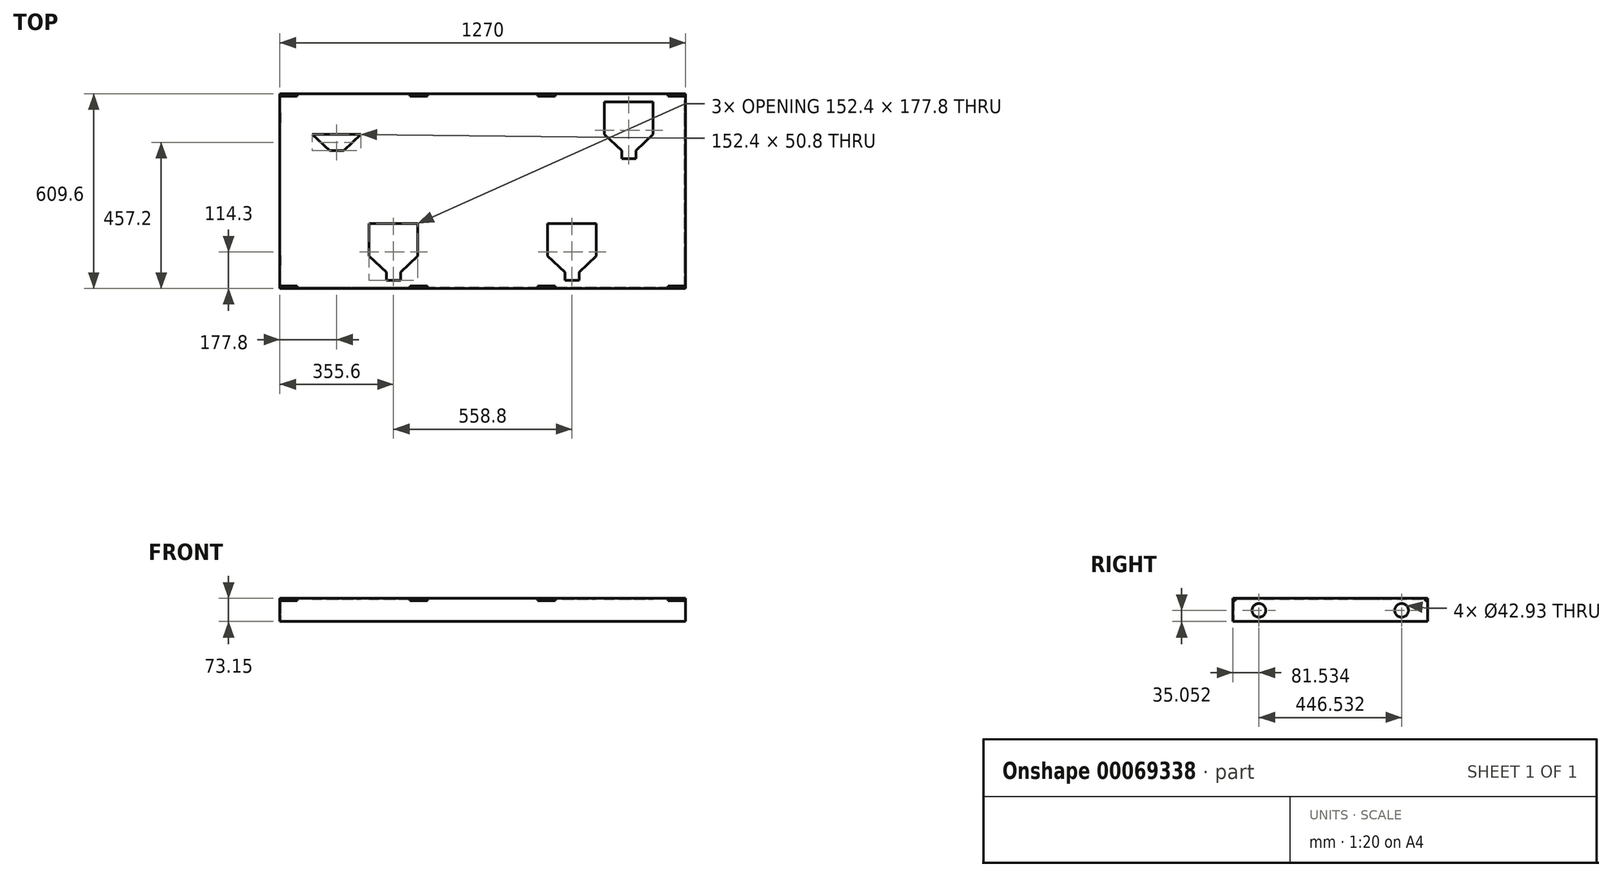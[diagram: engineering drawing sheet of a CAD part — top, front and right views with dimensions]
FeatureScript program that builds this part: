
annotation { "Feature Type Name" : "Feature", "Feature Type Description" : "" }
export const myFeature = defineFeature(function(context is Context, id is Id, definition is map)
    precondition{}
    {
        {
            var Q0;
            Q0=qCreatedBy(makeId("Top.planeOp"),FACE);
            var sketch = newSketch(context, id + "F0", { "sketchPlane" : qUnion([Q0])});
            skLineSegment(sketch, "E0.rect.bottom", {"start": v(635, -304.8) * mm, "end": v(-635, -304.8) * mm});
            skLineSegment(sketch, "E0.rect.top", {"start": v(635, 304.8) * mm, "end": v(-635, 304.8) * mm});
            skLineSegment(sketch, "E0.rect.left", {"start": v(635, -304.8) * mm, "end": v(635, 304.8) * mm});
            skLineSegment(sketch, "E0.rect.right", {"start": v(-635, -304.8) * mm, "end": v(-635, 304.8) * mm});
            skPoint(sketch, "E0.rect.middle", {"position": v(0, 0) * mm});
            skSolve(sketch);
        }
        {
            var Q0;
            Q0=makeQuery(id+"F0.imprint","IMPRINT",FACE,{"disambiguationData":[TD([[makeQuery(id+"F0.imprint","IMPRINT",EDGE,{"derivedFrom":sQuery(id+"F0.wireOp",EDGE,"E0.rect.bottom")}),-1.0]])]});
            extrude(context, id + "F1", {"entities" : qUnion([Q0]), "depth" : 73.15 * mm});
        }
        {
            var Q0;
            Q0=makeQuery(id+"F1.opExtrude","CAP_FACE",FACE,{"disambiguationData":[OSD([sQuery(id+"F0.wireOp",EDGE,"E0.rect.bottom"),sQuery(id+"F0.wireOp",EDGE,"E0.rect.top"),sQuery(id+"F0.wireOp",EDGE,"E0.rect.left"),sQuery(id+"F0.wireOp",EDGE,"E0.rect.right")])],"isStart":true});
            shell(context, id + "F2", {"entities" : qUnion([Q0]), "thickness" : 2.67 * mm});
        }
        {
            var Q0;
            Q0=makeQuery(id+"F1.opExtrude","CAP_FACE",FACE,{"disambiguationData":[OSD([sQuery(id+"F0.wireOp",EDGE,"E0.rect.bottom"),sQuery(id+"F0.wireOp",EDGE,"E0.rect.top"),sQuery(id+"F0.wireOp",EDGE,"E0.rect.left"),sQuery(id+"F0.wireOp",EDGE,"E0.rect.right")])],"isStart":false});
            var sketch = newSketch(context, id + "F3", { "sketchPlane" : qUnion([Q0])});
            skLineSegment(sketch, "E1.rect.bottom", {"start": v(-381, 101.6) * mm, "end": v(-533.4, 101.6) * mm});
            skLineSegment(sketch, "E1.rect.top", {"start": v(-381, 279.4) * mm, "end": v(-533.4, 279.4) * mm});
            skLineSegment(sketch, "E1.rect.left", {"start": v(-381, 101.6) * mm, "end": v(-381, 279.4) * mm});
            skLineSegment(sketch, "E1.rect.right", {"start": v(-533.4, 101.6) * mm, "end": v(-533.4, 279.4) * mm});
            skPoint(sketch, "E1.rect.middle", {"position": v(-457.2, 190.5) * mm});
            skLineSegment(sketch, "E2.bottom", {"start": v(-479.43, 101.6) * mm, "end": v(-434.98, 101.6) * mm});
            skLineSegment(sketch, "E2.top", {"start": v(-479.43, 127) * mm, "end": v(-434.98, 127) * mm});
            skLineSegment(sketch, "E2.left", {"start": v(-479.43, 101.6) * mm, "end": v(-479.43, 127) * mm});
            skLineSegment(sketch, "E2.right", {"start": v(-434.98, 101.6) * mm, "end": v(-434.98, 127) * mm});
            skLineSegment(sketch, "E3.bottom", {"start": v(-533.4, 279.4) * mm, "end": v(-381, 279.4) * mm});
            skLineSegment(sketch, "E3.top", {"start": v(-533.4, 177.8) * mm, "end": v(-381, 177.8) * mm});
            skLineSegment(sketch, "E3.left", {"start": v(-533.4, 279.4) * mm, "end": v(-533.4, 177.8) * mm});
            skLineSegment(sketch, "E3.right", {"start": v(-381, 279.4) * mm, "end": v(-381, 177.8) * mm});
            skLineSegment(sketch, "E4", {"start": v(-479.43, 127) * mm, "end": v(-533.4, 177.8) * mm});
            skLineSegment(sketch, "E5", {"start": v(-434.98, 127) * mm, "end": v(-381, 177.8) * mm});
            skPoint(sketch, "E6.rect.middle", {"position": v(-279.4, -190.5) * mm});
            skLineSegment(sketch, "E7", {"start": v(-301.62, -254) * mm, "end": v(-355.6, -203.2) * mm});
            skLineSegment(sketch, "E8.right", {"start": v(-203.2, -101.6) * mm, "end": v(-203.2, -203.2) * mm});
            skLineSegment(sketch, "E8.left", {"start": v(-355.6, -101.6) * mm, "end": v(-355.6, -203.2) * mm});
            skLineSegment(sketch, "E8.top", {"start": v(-355.6, -203.2) * mm, "end": v(-203.2, -203.2) * mm});
            skLineSegment(sketch, "E8.bottom", {"start": v(-355.6, -101.6) * mm, "end": v(-203.2, -101.6) * mm});
            skLineSegment(sketch, "E9.right", {"start": v(-257.17, -279.4) * mm, "end": v(-257.17, -254) * mm});
            skLineSegment(sketch, "E9.left", {"start": v(-301.62, -279.4) * mm, "end": v(-301.62, -254) * mm});
            skLineSegment(sketch, "E9.bottom", {"start": v(-301.62, -279.4) * mm, "end": v(-257.17, -279.4) * mm});
            skLineSegment(sketch, "E6.rect.right", {"start": v(-355.6, -279.4) * mm, "end": v(-355.6, -101.6) * mm});
            skLineSegment(sketch, "E9.top", {"start": v(-301.62, -254) * mm, "end": v(-257.17, -254) * mm});
            skLineSegment(sketch, "E10", {"start": v(-257.17, -254) * mm, "end": v(-203.2, -203.2) * mm});
            skLineSegment(sketch, "E6.rect.bottom", {"start": v(-203.2, -279.4) * mm, "end": v(-355.6, -279.4) * mm});
            skLineSegment(sketch, "E6.rect.left", {"start": v(-203.2, -279.4) * mm, "end": v(-203.2, -101.6) * mm});
            skLineSegment(sketch, "E6.rect.top", {"start": v(-203.2, -101.6) * mm, "end": v(-355.6, -101.6) * mm});
            skPoint(sketch, "E11.rect.middle", {"position": v(279.4, -190.5) * mm});
            skLineSegment(sketch, "E12", {"start": v(257.18, -254) * mm, "end": v(203.2, -203.2) * mm});
            skLineSegment(sketch, "E13.right", {"start": v(355.6, -101.6) * mm, "end": v(355.6, -203.2) * mm});
            skLineSegment(sketch, "E13.left", {"start": v(203.2, -101.6) * mm, "end": v(203.2, -203.2) * mm});
            skLineSegment(sketch, "E13.top", {"start": v(203.2, -203.2) * mm, "end": v(355.6, -203.2) * mm});
            skLineSegment(sketch, "E13.bottom", {"start": v(203.2, -101.6) * mm, "end": v(355.6, -101.6) * mm});
            skLineSegment(sketch, "E14.right", {"start": v(301.63, -279.4) * mm, "end": v(301.63, -254) * mm});
            skLineSegment(sketch, "E14.left", {"start": v(257.18, -279.4) * mm, "end": v(257.18, -254) * mm});
            skLineSegment(sketch, "E14.bottom", {"start": v(257.18, -279.4) * mm, "end": v(301.63, -279.4) * mm});
            skLineSegment(sketch, "E11.rect.right", {"start": v(203.2, -279.4) * mm, "end": v(203.2, -101.6) * mm});
            skLineSegment(sketch, "E14.top", {"start": v(257.18, -254) * mm, "end": v(301.63, -254) * mm});
            skLineSegment(sketch, "E15", {"start": v(301.63, -254) * mm, "end": v(355.6, -203.2) * mm});
            skLineSegment(sketch, "E11.rect.bottom", {"start": v(355.6, -279.4) * mm, "end": v(203.2, -279.4) * mm});
            skLineSegment(sketch, "E11.rect.left", {"start": v(355.6, -279.4) * mm, "end": v(355.6, -101.6) * mm});
            skLineSegment(sketch, "E11.rect.top", {"start": v(355.6, -101.6) * mm, "end": v(203.2, -101.6) * mm});
            skPoint(sketch, "E16.rect.middle", {"position": v(457.2, 190.5) * mm});
            skLineSegment(sketch, "E17", {"start": v(434.98, 127) * mm, "end": v(381, 177.8) * mm});
            skLineSegment(sketch, "E18.right", {"start": v(533.4, 279.4) * mm, "end": v(533.4, 177.8) * mm});
            skLineSegment(sketch, "E18.left", {"start": v(381, 279.4) * mm, "end": v(381, 177.8) * mm});
            skLineSegment(sketch, "E18.top", {"start": v(381, 177.8) * mm, "end": v(533.4, 177.8) * mm});
            skLineSegment(sketch, "E18.bottom", {"start": v(381, 279.4) * mm, "end": v(533.4, 279.4) * mm});
            skLineSegment(sketch, "E19.right", {"start": v(479.43, 101.6) * mm, "end": v(479.43, 127) * mm});
            skLineSegment(sketch, "E19.left", {"start": v(434.98, 101.6) * mm, "end": v(434.98, 127) * mm});
            skLineSegment(sketch, "E19.bottom", {"start": v(434.98, 101.6) * mm, "end": v(479.43, 101.6) * mm});
            skLineSegment(sketch, "E16.rect.right", {"start": v(381, 101.6) * mm, "end": v(381, 279.4) * mm});
            skLineSegment(sketch, "E19.top", {"start": v(434.98, 127) * mm, "end": v(479.43, 127) * mm});
            skLineSegment(sketch, "E20", {"start": v(479.42, 127) * mm, "end": v(533.4, 177.8) * mm});
            skLineSegment(sketch, "E16.rect.bottom", {"start": v(533.4, 101.6) * mm, "end": v(381, 101.6) * mm});
            skLineSegment(sketch, "E16.rect.left", {"start": v(533.4, 101.6) * mm, "end": v(533.4, 279.4) * mm});
            skLineSegment(sketch, "E16.rect.top", {"start": v(533.4, 279.4) * mm, "end": v(381, 279.4) * mm});
            skSolve(sketch);
        }
        {
            var Q0;
            Q0=makeQuery(id+"F3.imprint","IMPRINT",FACE,{"disambiguationData":[TD([[makeQuery(id+"F3.imprint","IMPRINT",EDGE,{"derivedFrom":sQuery(id+"F3.wireOp",EDGE,"E3.bottom")}),-1.0]])]});
            var Q1;
            Q1=makeQuery(id+"F3.imprint","IMPRINT",FACE,{"disambiguationData":[TD([[makeQuery(id+"F3.imprint","IMPRINT",EDGE,{"derivedFrom":sQuery(id+"F3.wireOp",EDGE,"E2.top")}),1.0]])]});
            var Q2;
            Q2=makeQuery(id+"F3.imprint","IMPRINT",FACE,{"disambiguationData":[TD([[makeQuery(id+"F3.imprint","IMPRINT",EDGE,{"derivedFrom":sQuery(id+"F3.wireOp",EDGE,"E2.bottom")}),1.0]])]});
            var Q3;
            {var subQ0=sQuery(id+"F3.wireOp",EDGE,"E8.top");Q3=makeQuery(id+"F3.imprint","IMPRINT",FACE,{"disambiguationData":[TD([[makeQuery(id+"F3.imprint","IMPRINT",EDGE,{"derivedFrom":subQ0}),1.0]])]});}
            var Q4;
            Q4=makeQuery(id+"F3.imprint","IMPRINT",FACE,{"disambiguationData":[TD([[makeQuery(id+"F3.imprint","IMPRINT",EDGE,{"derivedFrom":sQuery(id+"F3.wireOp",EDGE,"E7")}),-1.0]])]});
            var Q5;
            {var subQ0=sQuery(id+"F3.wireOp",EDGE,"E9.right");Q5=makeQuery(id+"F3.imprint","IMPRINT",FACE,{"disambiguationData":[TD([[makeQuery(id+"F3.imprint","IMPRINT",EDGE,{"derivedFrom":subQ0}),1.0]])]});}
            var Q6;
            {var subQ0=sQuery(id+"F3.wireOp",EDGE,"E14.right");Q6=makeQuery(id+"F3.imprint","IMPRINT",FACE,{"disambiguationData":[TD([[makeQuery(id+"F3.imprint","IMPRINT",EDGE,{"derivedFrom":subQ0}),1.0]])]});}
            var Q7;
            {var subQ0=sQuery(id+"F3.wireOp",EDGE,"E13.top");Q7=makeQuery(id+"F3.imprint","IMPRINT",FACE,{"disambiguationData":[TD([[makeQuery(id+"F3.imprint","IMPRINT",EDGE,{"derivedFrom":subQ0}),1.0]])]});}
            var Q8;
            {var subQ0=sQuery(id+"F3.wireOp",EDGE,"E19.right");Q8=makeQuery(id+"F3.imprint","IMPRINT",FACE,{"disambiguationData":[TD([[makeQuery(id+"F3.imprint","IMPRINT",EDGE,{"derivedFrom":subQ0}),1.0]])]});}
            var Q9;
            Q9=makeQuery(id+"F3.imprint","IMPRINT",FACE,{"disambiguationData":[TD([[makeQuery(id+"F3.imprint","IMPRINT",EDGE,{"derivedFrom":sQuery(id+"F3.wireOp",EDGE,"E17")}),-1.0]])]});
            var Q10;
            {var subQ0=sQuery(id+"F3.wireOp",EDGE,"E18.top");Q10=makeQuery(id+"F3.imprint","IMPRINT",FACE,{"disambiguationData":[TD([[makeQuery(id+"F3.imprint","IMPRINT",EDGE,{"derivedFrom":subQ0}),1.0]])]});}
            var Q11;
            Q11=makeQuery(id+"F3.imprint","IMPRINT",FACE,{"disambiguationData":[TD([[makeQuery(id+"F3.imprint","IMPRINT",EDGE,{"derivedFrom":sQuery(id+"F3.wireOp",EDGE,"E12")}),-1.0]])]});
            extrude(context, id + "F4", {"entities" : qUnion([Q0, Q1, Q2, Q3, Q4, Q5, Q6, Q7, Q8, Q9, Q10, Q11]), "operationType" : NewBodyOperationType.REMOVE, "endBound" : BoundingType.THROUGH_ALL, "oppositeDirection" : true, "depth" : 25.4 * mm});
        }
        {
            var Q0;
            Q0=makeQuery(id+"F1.opExtrude","CAP_FACE",FACE,{"disambiguationData":[OSD([sQuery(id+"F0.wireOp",EDGE,"E0.rect.bottom"),sQuery(id+"F0.wireOp",EDGE,"E0.rect.top"),sQuery(id+"F0.wireOp",EDGE,"E0.rect.left"),sQuery(id+"F0.wireOp",EDGE,"E0.rect.right")])],"isStart":false});
            var sketch = newSketch(context, id + "F5", { "sketchPlane" : qUnion([Q0])});
            skLineSegment(sketch, "E21.bottom", {"start": v(-635, 304.8) * mm, "end": v(-580.9, 304.8) * mm});
            skLineSegment(sketch, "E21.top", {"start": v(-635, 296.93) * mm, "end": v(-580.9, 296.93) * mm});
            skLineSegment(sketch, "E21.left", {"start": v(-635, 304.8) * mm, "end": v(-635, 296.93) * mm});
            skLineSegment(sketch, "E21.right", {"start": v(-580.9, 304.8) * mm, "end": v(-580.9, 296.93) * mm});
            skLineSegment(sketch, "E22.bottom", {"start": v(-227.08, 304.8) * mm, "end": v(-172.97, 304.8) * mm});
            skLineSegment(sketch, "E22.top", {"start": v(-227.08, 296.93) * mm, "end": v(-172.97, 296.93) * mm});
            skLineSegment(sketch, "E22.left", {"start": v(-227.08, 304.8) * mm, "end": v(-227.08, 296.93) * mm});
            skLineSegment(sketch, "E22.right", {"start": v(-172.97, 304.8) * mm, "end": v(-172.97, 296.93) * mm});
            skLineSegment(sketch, "E23.bottom", {"start": v(172.97, 304.8) * mm, "end": v(227.08, 304.8) * mm});
            skLineSegment(sketch, "E23.top", {"start": v(172.97, 296.93) * mm, "end": v(227.08, 296.93) * mm});
            skLineSegment(sketch, "E23.left", {"start": v(172.97, 304.8) * mm, "end": v(172.97, 296.93) * mm});
            skLineSegment(sketch, "E23.right", {"start": v(227.08, 304.8) * mm, "end": v(227.08, 296.93) * mm});
            skLineSegment(sketch, "E24.bottom", {"start": v(635, 304.8) * mm, "end": v(580.9, 304.8) * mm});
            skLineSegment(sketch, "E24.top", {"start": v(635, 296.93) * mm, "end": v(580.9, 296.93) * mm});
            skLineSegment(sketch, "E24.left", {"start": v(635, 304.8) * mm, "end": v(635, 296.93) * mm});
            skLineSegment(sketch, "E24.right", {"start": v(580.9, 304.8) * mm, "end": v(580.9, 296.93) * mm});
            skLineSegment(sketch, "E25.bottom", {"start": v(635, -304.8) * mm, "end": v(580.9, -304.8) * mm});
            skLineSegment(sketch, "E25.top", {"start": v(635, -296.93) * mm, "end": v(580.9, -296.93) * mm});
            skLineSegment(sketch, "E25.left", {"start": v(635, -304.8) * mm, "end": v(635, -296.93) * mm});
            skLineSegment(sketch, "E25.right", {"start": v(580.9, -304.8) * mm, "end": v(580.9, -296.93) * mm});
            skLineSegment(sketch, "E26.bottom", {"start": v(227.08, -304.8) * mm, "end": v(172.97, -304.8) * mm});
            skLineSegment(sketch, "E26.top", {"start": v(227.08, -296.93) * mm, "end": v(172.97, -296.93) * mm});
            skLineSegment(sketch, "E26.left", {"start": v(227.08, -304.8) * mm, "end": v(227.08, -296.93) * mm});
            skLineSegment(sketch, "E26.right", {"start": v(172.97, -304.8) * mm, "end": v(172.97, -296.93) * mm});
            skLineSegment(sketch, "E27.bottom", {"start": v(-172.97, -304.8) * mm, "end": v(-227.08, -304.8) * mm});
            skLineSegment(sketch, "E27.top", {"start": v(-172.97, -296.93) * mm, "end": v(-227.08, -296.93) * mm});
            skLineSegment(sketch, "E27.left", {"start": v(-172.97, -304.8) * mm, "end": v(-172.97, -296.93) * mm});
            skLineSegment(sketch, "E27.right", {"start": v(-227.08, -304.8) * mm, "end": v(-227.08, -296.93) * mm});
            skLineSegment(sketch, "E28.bottom", {"start": v(-635, -304.8) * mm, "end": v(-580.9, -304.8) * mm});
            skLineSegment(sketch, "E28.top", {"start": v(-635, -296.93) * mm, "end": v(-580.9, -296.93) * mm});
            skLineSegment(sketch, "E28.left", {"start": v(-635, -304.8) * mm, "end": v(-635, -296.93) * mm});
            skLineSegment(sketch, "E28.right", {"start": v(-580.9, -304.8) * mm, "end": v(-580.9, -296.93) * mm});
            skSolve(sketch);
        }
        {
            var Q0;
            Q0=makeQuery(id+"F5.imprint","IMPRINT",FACE,{"disambiguationData":[TD([[makeQuery(id+"F5.imprint","IMPRINT",EDGE,{"derivedFrom":sQuery(id+"F5.wireOp",EDGE,"E21.bottom")}),1.0]])]});
            var Q1;
            Q1=makeQuery(id+"F5.imprint","IMPRINT",FACE,{"disambiguationData":[TD([[makeQuery(id+"F5.imprint","IMPRINT",EDGE,{"derivedFrom":sQuery(id+"F5.wireOp",EDGE,"E22.bottom")}),1.0]])]});
            var Q2;
            Q2=makeQuery(id+"F5.imprint","IMPRINT",FACE,{"disambiguationData":[TD([[makeQuery(id+"F5.imprint","IMPRINT",EDGE,{"derivedFrom":sQuery(id+"F5.wireOp",EDGE,"E23.bottom")}),1.0]])]});
            var Q3;
            Q3=makeQuery(id+"F5.imprint","IMPRINT",FACE,{"disambiguationData":[TD([[makeQuery(id+"F5.imprint","IMPRINT",EDGE,{"derivedFrom":sQuery(id+"F5.wireOp",EDGE,"E24.bottom")}),1.0]])]});
            var Q4;
            Q4=makeQuery(id+"F5.imprint","IMPRINT",FACE,{"disambiguationData":[TD([[makeQuery(id+"F5.imprint","IMPRINT",EDGE,{"derivedFrom":sQuery(id+"F5.wireOp",EDGE,"E25.bottom")}),-1.0]])]});
            var Q5;
            Q5=makeQuery(id+"F5.imprint","IMPRINT",FACE,{"disambiguationData":[TD([[makeQuery(id+"F5.imprint","IMPRINT",EDGE,{"derivedFrom":sQuery(id+"F5.wireOp",EDGE,"E26.bottom")}),-1.0]])]});
            var Q6;
            Q6=makeQuery(id+"F5.imprint","IMPRINT",FACE,{"disambiguationData":[TD([[makeQuery(id+"F5.imprint","IMPRINT",EDGE,{"derivedFrom":sQuery(id+"F5.wireOp",EDGE,"E27.bottom")}),-1.0]])]});
            var Q7;
            Q7=makeQuery(id+"F5.imprint","IMPRINT",FACE,{"disambiguationData":[TD([[makeQuery(id+"F5.imprint","IMPRINT",EDGE,{"derivedFrom":sQuery(id+"F5.wireOp",EDGE,"E28.bottom")}),-1.0]])]});
            extrude(context, id + "F6", {"entities" : qUnion([Q0, Q1, Q2, Q3, Q4, Q5, Q6, Q7]), "operationType" : NewBodyOperationType.REMOVE, "oppositeDirection" : true, "depth" : 7.87 * mm});
        }
        {
            var Q0;
            Q0=makeQuery(id+"F1.opExtrude","SWEPT_FACE",FACE,{"disambiguationData":[OSD([sQuery(id+"F0.wireOp",EDGE,"E0.rect.left")])]});
            var sketch = newSketch(context, id + "F7", { "sketchPlane" : qUnion([Q0])});
            skCircle(sketch, "E29", {"center": v(223.27, 35.05) * mm, "radius": 21.46 * mm});
            skCircle(sketch, "E30", {"center": v(-223.27, 35.05) * mm, "radius": 21.46 * mm});
            skSolve(sketch);
        }
        {
            var Q0;
            Q0=makeQuery(id+"F7.imprint","IMPRINT",FACE,{"disambiguationData":[TD([[makeQuery(id+"F7.imprint","IMPRINT",EDGE,{"derivedFrom":sQuery(id+"F7.wireOp",EDGE,"E29")}),1.0]])]});
            var Q1;
            Q1=makeQuery(id+"F7.imprint","IMPRINT",FACE,{"disambiguationData":[TD([[makeQuery(id+"F7.imprint","IMPRINT",EDGE,{"derivedFrom":sQuery(id+"F7.wireOp",EDGE,"E30")}),1.0]])]});
            extrude(context, id + "F8", {"entities" : qUnion([Q0, Q1]), "operationType" : NewBodyOperationType.REMOVE, "endBound" : BoundingType.THROUGH_ALL, "oppositeDirection" : true, "depth" : 25.4 * mm});
        }
    });
